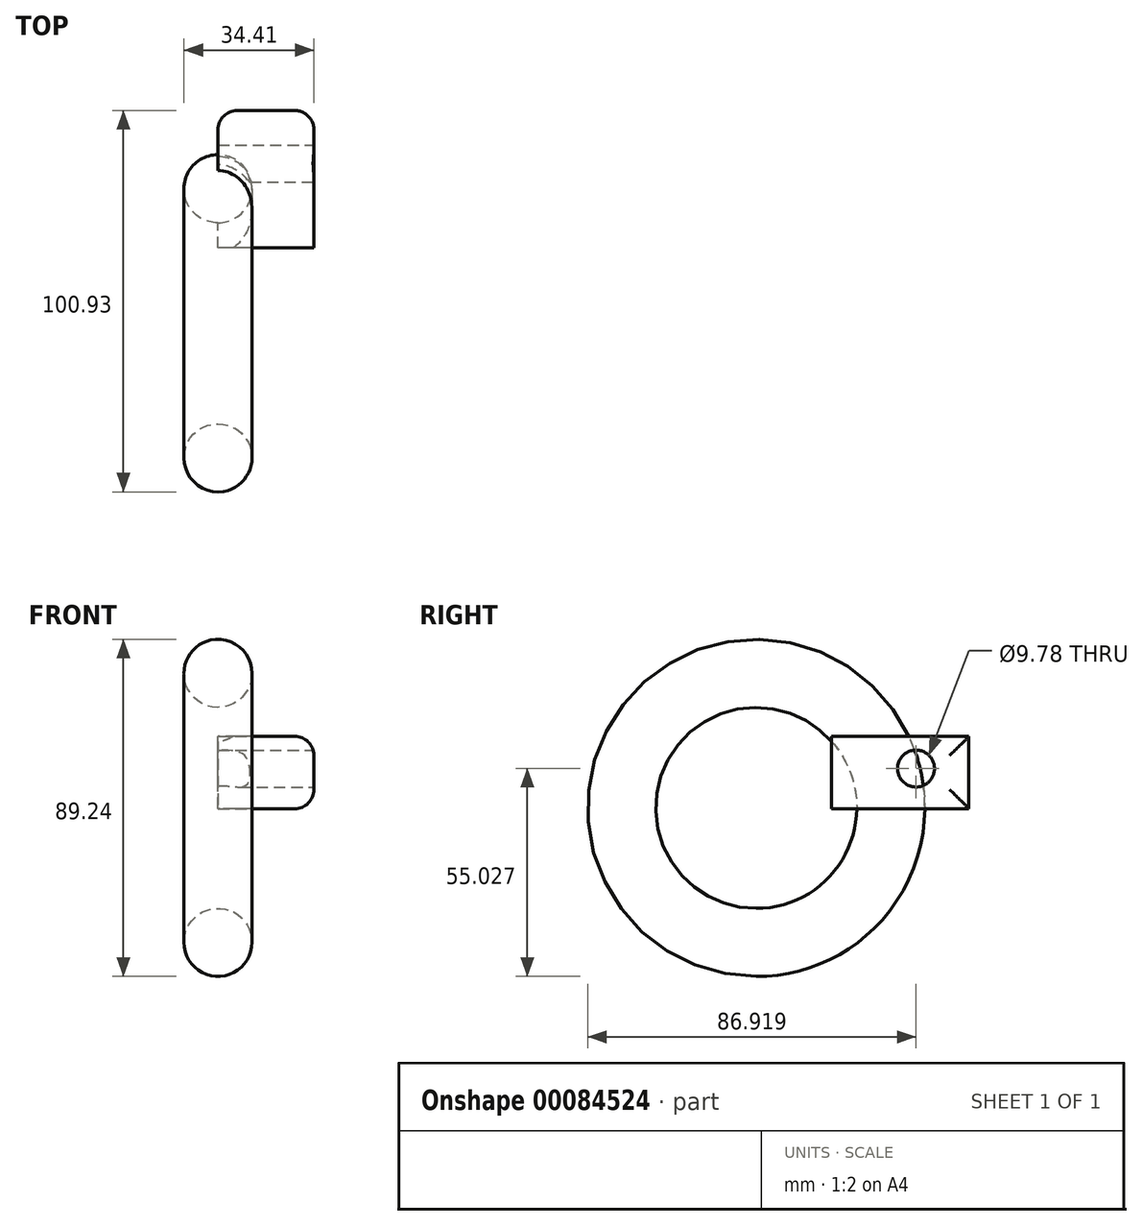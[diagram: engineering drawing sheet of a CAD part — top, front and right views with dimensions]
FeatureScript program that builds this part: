
annotation { "Feature Type Name" : "Feature", "Feature Type Description" : "" }
export const myFeature = defineFeature(function(context is Context, id is Id, definition is map)
    precondition{}
    {
        {
            var Q0;
            Q0=qCreatedBy(makeId("Right.planeOp"),FACE);
            var sketch = newSketch(context, id + "F0", { "sketchPlane" : qUnion([Q0])});
            skLineSegment(sketch, "E0.bottom", {"start": v(0, 0) * mm, "end": v(36.35, 0) * mm});
            skLineSegment(sketch, "E0.top", {"start": v(0, 19.18) * mm, "end": v(36.35, 19.18) * mm});
            skLineSegment(sketch, "E0.left", {"start": v(0, 0) * mm, "end": v(0, 19.18) * mm});
            skLineSegment(sketch, "E0.right", {"start": v(36.35, 0) * mm, "end": v(36.35, 19.18) * mm});
            skSolve(sketch);
        }
        {
            var Q0;
            Q0 = qSketchRegion(id + "F0", true);
            extrude(context, id + "F1", {"entities" : qUnion([Q0]), "depth" : 25.4 * mm});
        }
        {
            var Q0;
            Q0=makeQuery(id+"F1.opExtrude","CAP_FACE",FACE,{"disambiguationData":[OSD([sQuery(id+"F0.wireOp",EDGE,"E0.bottom"),sQuery(id+"F0.wireOp",EDGE,"E0.top"),sQuery(id+"F0.wireOp",EDGE,"E0.left"),sQuery(id+"F0.wireOp",EDGE,"E0.right")])],"isStart":false});
            var sketch = newSketch(context, id + "F2", { "sketchPlane" : qUnion([Q0])});
            skCircle(sketch, "E1", {"center": v(22.34, 10.65) * mm, "radius": 4.9 * mm});
            skSolve(sketch);
        }
        {
            var Q0;
            Q0 = qSketchRegion(id + "F2", true);
            extrude(context, id + "F3", {"entities" : qUnion([Q0]), "operationType" : NewBodyOperationType.REMOVE, "oppositeDirection" : true, "depth" : 25.4 * mm});
        }
        {
            var Q0;
            Q0=makeQuery(id+"F1.opExtrude","CAP_EDGE",EDGE,{"disambiguationData":[OSD([sQuery(id+"F0.wireOp",EDGE,"E0.bottom")])],"isStart":false});
            var Q1;
            Q1=makeQuery(id+"F1.opExtrude","CAP_EDGE",EDGE,{"disambiguationData":[OSD([sQuery(id+"F0.wireOp",EDGE,"E0.top")])],"isStart":false});
            var Q2;
            Q2=makeQuery(id+"F1.opExtrude","CAP_EDGE",EDGE,{"disambiguationData":[OSD([sQuery(id+"F0.wireOp",EDGE,"E0.right")])],"isStart":false});
            var Q3;
            Q3=makeQuery(id+"F1.opExtrude","CAP_EDGE",EDGE,{"disambiguationData":[OSD([sQuery(id+"F0.wireOp",EDGE,"E0.right")])],"isStart":true});
            fillet(context, id + "F4", {"entities" : qUnion([Q0, Q1, Q2, Q3]), "radius" : 5.08 * mm, "tangentPropagation" : true, "allowEdgeOverflow" : false});
        }
        {
            var Q0;
            Q0=qCreatedBy(makeId("Top.planeOp"),FACE);
            var sketch = newSketch(context, id + "F5", { "sketchPlane" : qUnion([Q0])});
            skCircle(sketch, "E2", {"center": v(0, -55.56) * mm, "radius": 9.01 * mm});
            skSolve(sketch);
        }
        {
            var Q0;
            Q0=qCreatedBy(makeId("Right.planeOp"),FACE);
            var sketch = newSketch(context, id + "F6", { "sketchPlane" : qUnion([Q0])});
            skCircle(sketch, "E3", {"center": v(-19.96, 0.24) * mm, "radius": 35.54 * mm});
            skPoint(sketch, "E3.first.point", {"position": v(-55.5, 0) * mm});
            skPoint(sketch, "E3.second.point", {"position": v(15.45, -2.76) * mm});
            skPoint(sketch, "E3.third.point", {"position": v(-10.93, -34.13) * mm});
            skSolve(sketch);
        }
        {
            var Q0;
            Q0=makeQuery(id+"F5.imprint","IMPRINT",FACE,{"disambiguationData":[TD([[makeQuery(id+"F5.imprint","IMPRINT",EDGE,{"derivedFrom":sQuery(id+"F5.wireOp",EDGE,"E2")}),1.0]])]});
            var Q1;
            Q1=sQuery(id+"F6.wireOp",EDGE,"E3");
            revolve(context, id + "F7", {"operationType" : NewBodyOperationType.ADD, "entities" : qUnion([Q0]), "axis" : qUnion([Q1]), "revolveType" : RevolveType.FULL});
        }
    });
